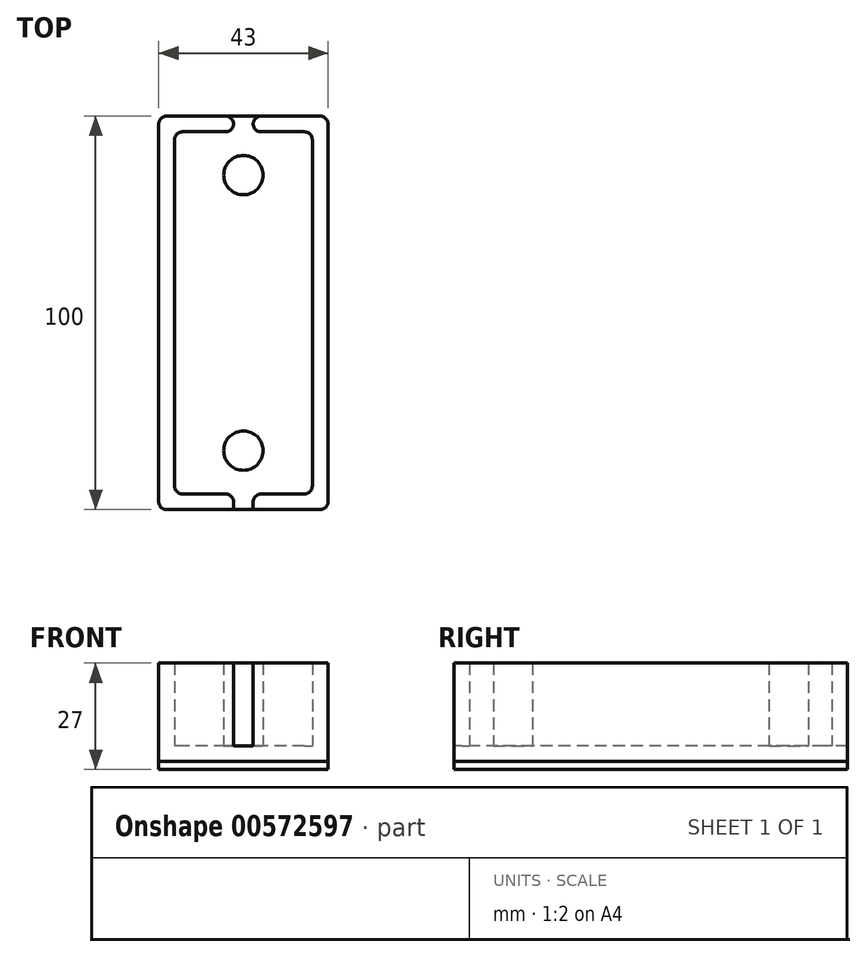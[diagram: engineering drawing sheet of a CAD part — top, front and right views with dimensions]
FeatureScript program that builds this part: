
annotation { "Feature Type Name" : "Feature", "Feature Type Description" : "" }
export const myFeature = defineFeature(function(context is Context, id is Id, definition is map)
    precondition{}
    {
        {
            var Q0;
            Q0=qCreatedBy(makeId("Top.planeOp"),FACE);
            var sketch = newSketch(context, id + "F0", { "sketchPlane" : qUnion([Q0])});
            skLineSegment(sketch, "E0.bottom", {"start": v(21.5, 50) * mm, "end": v(-21.5, 50) * mm});
            skLineSegment(sketch, "E0.top", {"start": v(21.5, -50) * mm, "end": v(-21.5, -50) * mm});
            skLineSegment(sketch, "E0.left", {"start": v(21.5, 50) * mm, "end": v(21.5, -50) * mm});
            skLineSegment(sketch, "E0.right", {"start": v(-21.5, 50) * mm, "end": v(-21.5, -50) * mm});
            skPoint(sketch, "E0.middle", {"position": v(0, 0) * mm});
            skSolve(sketch);
        }
        {
            var Q0;
            Q0 = qSketchRegion(id + "F0", true);
            extrude(context, id + "F1", {"entities" : qUnion([Q0]), "depth" : 25 * mm, "offsetDistance" : 25 * mm});
        }
        {
            var Q0;
            Q0=makeQuery(id+"F1.opExtrude","CAP_FACE",FACE,{"disambiguationData":[OSD([sQuery(id+"F0.wireOp",EDGE,"E0.bottom"),sQuery(id+"F0.wireOp",EDGE,"E0.top"),sQuery(id+"F0.wireOp",EDGE,"E0.left"),sQuery(id+"F0.wireOp",EDGE,"E0.right")])],"isStart":false});
            var Q1;
            Q1=makeQuery(id+"F1.opExtrude","SWEPT_BODY",BODY,{"disambiguationData":[OSD([sQuery(id+"F0.wireOp",EDGE,"E0.bottom"),sQuery(id+"F0.wireOp",EDGE,"E0.top"),sQuery(id+"F0.wireOp",EDGE,"E0.left"),sQuery(id+"F0.wireOp",EDGE,"E0.right")])]});
            shell(context, id + "F2", {"entities" : qUnion([Q0]), "parts" : qUnion([Q1]), "thickness" : 4 * mm});
        }
        {
            var Q0;
            Q0=makeQuery(id+"F2.opShell","OFFSET_FACE",FACE,{"disambiguationData":[OSD([sQuery(id+"F0.wireOp",EDGE,"E0.bottom"),sQuery(id+"F0.wireOp",EDGE,"E0.top"),sQuery(id+"F0.wireOp",EDGE,"E0.left"),sQuery(id+"F0.wireOp",EDGE,"E0.right")])]});
            var sketch = newSketch(context, id + "F3", { "sketchPlane" : qUnion([Q0])});
            skCircle(sketch, "E1", {"center": v(0, 35) * mm, "radius": 5 * mm});
            skCircle(sketch, "E2", {"center": v(0, -35) * mm, "radius": 5 * mm});
            skSolve(sketch);
        }
        {
            var Q0;
            Q0 = qSketchRegion(id + "F3", true);
            var Q1;
            Q1=makeQuery(id+"F1.opExtrude","CAP_FACE",FACE,{"disambiguationData":[OSD([sQuery(id+"F0.wireOp",EDGE,"E0.bottom"),sQuery(id+"F0.wireOp",EDGE,"E0.top"),sQuery(id+"F0.wireOp",EDGE,"E0.left"),sQuery(id+"F0.wireOp",EDGE,"E0.right")])],"isStart":false});
            extrude(context, id + "F4", {"entities" : qUnion([Q0]), "operationType" : NewBodyOperationType.ADD, "endBound" : BoundingType.UP_TO_SURFACE, "depth" : 25 * mm, "endBoundEntityFace" : qUnion([Q1]), "offsetDistance" : 25 * mm});
        }
        {
            var Q0;
            Q0=makeQuery(id+"F1.opExtrude","CAP_FACE",FACE,{"disambiguationData":[OSD([sQuery(id+"F0.wireOp",EDGE,"E0.bottom"),sQuery(id+"F0.wireOp",EDGE,"E0.top"),sQuery(id+"F0.wireOp",EDGE,"E0.left"),sQuery(id+"F0.wireOp",EDGE,"E0.right")])],"isStart":false});
            var sketch = newSketch(context, id + "F5", { "sketchPlane" : qUnion([Q0])});
            skLineSegment(sketch, "E3.bottom", {"start": v(-2.5, 51) * mm, "end": v(2.5, 51) * mm});
            skLineSegment(sketch, "E3.top", {"start": v(-2.5, 41) * mm, "end": v(2.5, 41) * mm});
            skLineSegment(sketch, "E3.left", {"start": v(-2.5, 51) * mm, "end": v(-2.5, 41) * mm});
            skLineSegment(sketch, "E3.right", {"start": v(2.5, 51) * mm, "end": v(2.5, 41) * mm});
            skPoint(sketch, "E3.middle", {"position": v(0, 46) * mm});
            skLineSegment(sketch, "E4.bottom", {"start": v(-2.5, -50) * mm, "end": v(2.5, -50) * mm});
            skLineSegment(sketch, "E4.top", {"start": v(-2.5, -42) * mm, "end": v(2.5, -42) * mm});
            skLineSegment(sketch, "E4.left", {"start": v(-2.5, -50) * mm, "end": v(-2.5, -42) * mm});
            skLineSegment(sketch, "E4.right", {"start": v(2.5, -50) * mm, "end": v(2.5, -42) * mm});
            skPoint(sketch, "E4.middle", {"position": v(0, -46) * mm});
            skSolve(sketch);
        }
        {
            var Q0;
            Q0 = qSketchRegion(id + "F5", true);
            var Q1;
            Q1=makeQuery(id+"F2.opShell","OFFSET_FACE",FACE,{"disambiguationData":[OSD([sQuery(id+"F0.wireOp",EDGE,"E0.bottom"),sQuery(id+"F0.wireOp",EDGE,"E0.top"),sQuery(id+"F0.wireOp",EDGE,"E0.left"),sQuery(id+"F0.wireOp",EDGE,"E0.right")])]});
            extrude(context, id + "F6", {"entities" : qUnion([Q0]), "operationType" : NewBodyOperationType.REMOVE, "endBound" : BoundingType.UP_TO_SURFACE, "oppositeDirection" : true, "depth" : 25 * mm, "endBoundEntityFace" : qUnion([Q1]), "offsetDistance" : 25 * mm});
        }
        {
            var Q0;
            Q0=makeQuery(id+"F6.boolean.opBoolean","INTERSECT",EDGE,{"derivedFrom":[makeQuery(id+"F2.opShell","OFFSET_FACE",FACE,{"disambiguationData":[OSD([sQuery(id+"F0.wireOp",EDGE,"E0.top")])]}),makeQuery(id+"F6.opExtrude","SWEPT_FACE",FACE,{"disambiguationData":[OSD([sQuery(id+"F5.wireOp",EDGE,"E4.left")])]})]});
            var Q1;
            Q1=makeQuery(id+"F6.boolean.opBoolean","COPY",EDGE,{"derivedFrom":makeQuery(id+"F6.opExtrude","SWEPT_EDGE",EDGE,{"disambiguationData":[OSD([sQuery(id+"F0.wireOp",EDGE,"E0.top"),sQuery(id+"F5.wireOp",EDGE,"E4.bottom"),sQuery(id+"F5.wireOp",EDGE,"E4.left")])]})});
            var Q2;
            Q2=makeQuery(id+"F6.boolean.opBoolean","COPY",EDGE,{"derivedFrom":makeQuery(id+"F6.opExtrude","SWEPT_EDGE",EDGE,{"disambiguationData":[OSD([sQuery(id+"F0.wireOp",EDGE,"E0.top"),sQuery(id+"F5.wireOp",EDGE,"E4.bottom"),sQuery(id+"F5.wireOp",EDGE,"E4.right")])]})});
            var Q3;
            Q3=makeQuery(id+"F6.boolean.opBoolean","INTERSECT",EDGE,{"derivedFrom":[makeQuery(id+"F1.opExtrude","SWEPT_FACE",FACE,{"disambiguationData":[OSD([sQuery(id+"F0.wireOp",EDGE,"E0.bottom")])]}),makeQuery(id+"F6.opExtrude","SWEPT_FACE",FACE,{"disambiguationData":[OSD([sQuery(id+"F5.wireOp",EDGE,"E3.left")])]})]});
            var Q4;
            Q4=makeQuery(id+"F6.boolean.opBoolean","INTERSECT",EDGE,{"derivedFrom":[makeQuery(id+"F2.opShell","OFFSET_FACE",FACE,{"disambiguationData":[OSD([sQuery(id+"F0.wireOp",EDGE,"E0.bottom")])]}),makeQuery(id+"F6.opExtrude","SWEPT_FACE",FACE,{"disambiguationData":[OSD([sQuery(id+"F5.wireOp",EDGE,"E3.left")])]})]});
            var Q5;
            Q5=makeQuery(id+"F6.boolean.opBoolean","INTERSECT",EDGE,{"derivedFrom":[makeQuery(id+"F2.opShell","OFFSET_FACE",FACE,{"disambiguationData":[OSD([sQuery(id+"F0.wireOp",EDGE,"E0.bottom")])]}),makeQuery(id+"F6.opExtrude","SWEPT_FACE",FACE,{"disambiguationData":[OSD([sQuery(id+"F5.wireOp",EDGE,"E3.right")])]})]});
            var Q6;
            Q6=makeQuery(id+"F6.boolean.opBoolean","INTERSECT",EDGE,{"derivedFrom":[makeQuery(id+"F2.opShell","OFFSET_FACE",FACE,{"disambiguationData":[OSD([sQuery(id+"F0.wireOp",EDGE,"E0.top")])]}),makeQuery(id+"F6.opExtrude","SWEPT_FACE",FACE,{"disambiguationData":[OSD([sQuery(id+"F5.wireOp",EDGE,"E4.right")])]})]});
            var Q7;
            Q7=makeQuery(id+"F6.boolean.opBoolean","INTERSECT",EDGE,{"derivedFrom":[makeQuery(id+"F1.opExtrude","SWEPT_FACE",FACE,{"disambiguationData":[OSD([sQuery(id+"F0.wireOp",EDGE,"E0.bottom")])]}),makeQuery(id+"F6.opExtrude","SWEPT_FACE",FACE,{"disambiguationData":[OSD([sQuery(id+"F5.wireOp",EDGE,"E3.right")])]})]});
            var Q8;
            Q8=makeQuery(id+"F2.opShell","OFFSET_EDGE",EDGE,{"disambiguationData":[OSD([sQuery(id+"F0.wireOp",EDGE,"E0.bottom"),sQuery(id+"F0.wireOp",EDGE,"E0.left")])]});
            var Q9;
            Q9=makeQuery(id+"F2.opShell","OFFSET_EDGE",EDGE,{"disambiguationData":[OSD([sQuery(id+"F0.wireOp",EDGE,"E0.top"),sQuery(id+"F0.wireOp",EDGE,"E0.left")])]});
            var Q10;
            Q10=makeQuery(id+"F2.opShell","OFFSET_EDGE",EDGE,{"disambiguationData":[OSD([sQuery(id+"F0.wireOp",EDGE,"E0.top"),sQuery(id+"F0.wireOp",EDGE,"E0.right")])]});
            var Q11;
            Q11=makeQuery(id+"F2.opShell","OFFSET_EDGE",EDGE,{"disambiguationData":[OSD([sQuery(id+"F0.wireOp",EDGE,"E0.bottom"),sQuery(id+"F0.wireOp",EDGE,"E0.right")])]});
            var Q12;
            Q12=makeQuery(id+"F1.opExtrude","SWEPT_EDGE",EDGE,{"disambiguationData":[OSD([sQuery(id+"F0.wireOp",EDGE,"E0.top"),sQuery(id+"F0.wireOp",EDGE,"E0.right")])]});
            var Q13;
            Q13=makeQuery(id+"F1.opExtrude","SWEPT_EDGE",EDGE,{"disambiguationData":[OSD([sQuery(id+"F0.wireOp",EDGE,"E0.top"),sQuery(id+"F0.wireOp",EDGE,"E0.left")])]});
            var Q14;
            Q14=makeQuery(id+"F1.opExtrude","SWEPT_EDGE",EDGE,{"disambiguationData":[OSD([sQuery(id+"F0.wireOp",EDGE,"E0.bottom"),sQuery(id+"F0.wireOp",EDGE,"E0.left")])]});
            var Q15;
            Q15=makeQuery(id+"F1.opExtrude","SWEPT_EDGE",EDGE,{"disambiguationData":[OSD([sQuery(id+"F0.wireOp",EDGE,"E0.bottom"),sQuery(id+"F0.wireOp",EDGE,"E0.right")])]});
            fillet(context, id + "F7", {"entities" : qUnion([Q0, Q1, Q2, Q3, Q4, Q5, Q6, Q7, Q8, Q9, Q10, Q11, Q12, Q13, Q14, Q15]), "radius" : 2 * mm, "tangentPropagation" : true, "allowEdgeOverflow" : false});
        }
        {
            var Q0;
            Q0=makeQuery(id+"F1.opExtrude","CAP_FACE",FACE,{"disambiguationData":[OSD([sQuery(id+"F0.wireOp",EDGE,"E0.bottom"),sQuery(id+"F0.wireOp",EDGE,"E0.top"),sQuery(id+"F0.wireOp",EDGE,"E0.left"),sQuery(id+"F0.wireOp",EDGE,"E0.right")])],"isStart":true});
            extrude(context, id + "F8", {"entities" : qUnion([Q0]), "depth" : 2 * mm, "offsetDistance" : 25 * mm});
        }
    });
